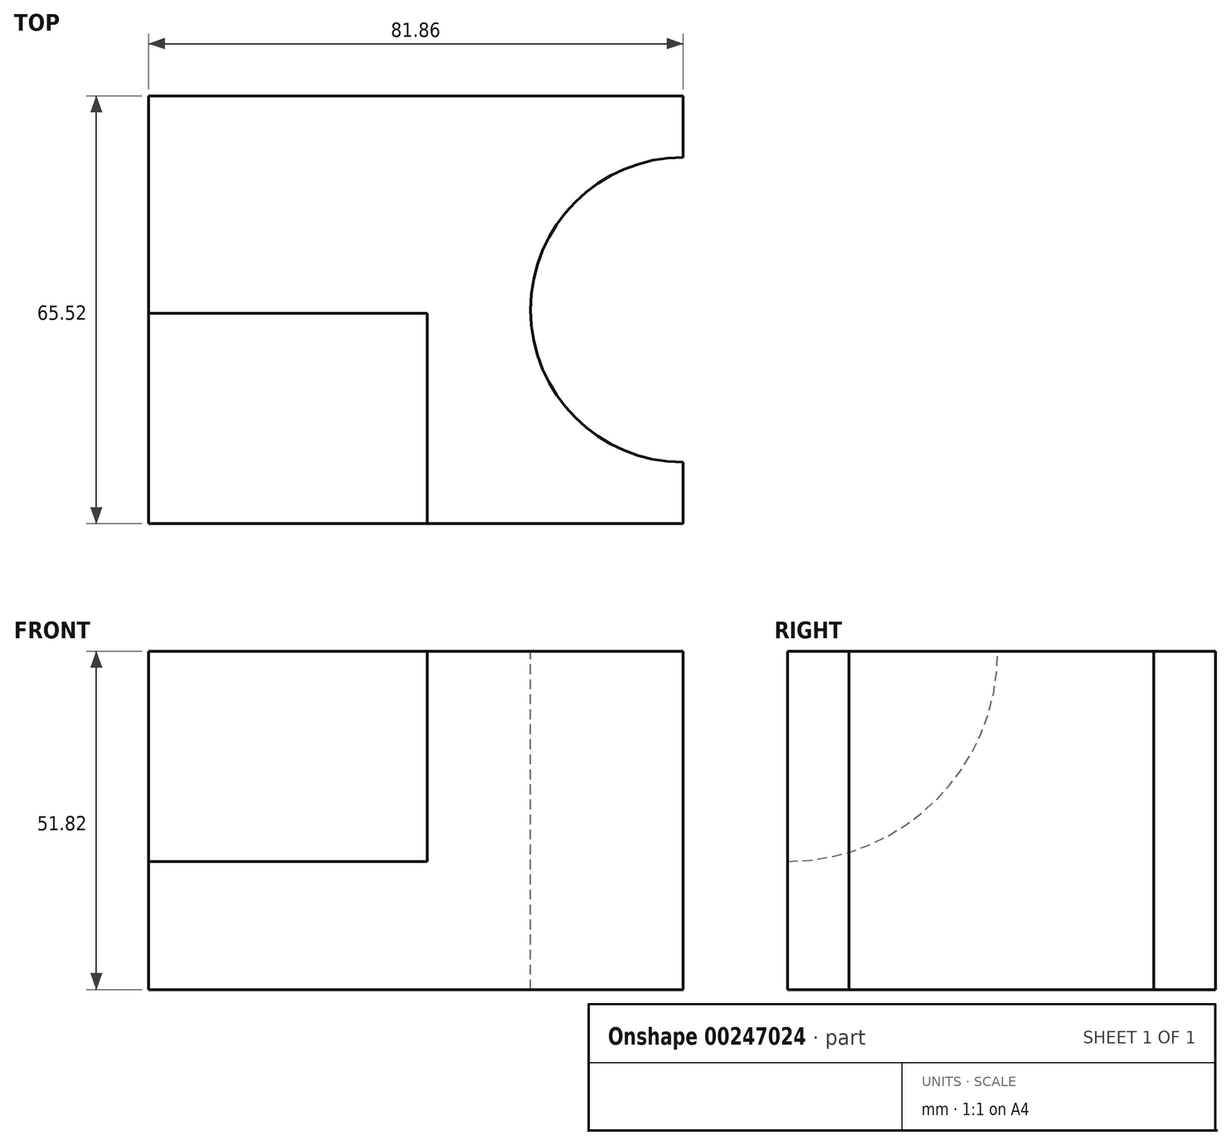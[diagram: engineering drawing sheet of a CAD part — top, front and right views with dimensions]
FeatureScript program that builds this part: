
annotation { "Feature Type Name" : "Feature", "Feature Type Description" : "" }
export const myFeature = defineFeature(function(context is Context, id is Id, definition is map)
    precondition{}
    {
        {
            var Q0;
            Q0=qCreatedBy(makeId("Top.planeOp"),FACE);
            var sketch = newSketch(context, id + "F0", { "sketchPlane" : qUnion([Q0])});
            skLineSegment(sketch, "E0.bottom", {"start": v(-40.93, 32.76) * mm, "end": v(40.93, 32.76) * mm});
            skLineSegment(sketch, "E0.top", {"start": v(-40.93, -32.76) * mm, "end": v(40.93, -32.76) * mm});
            skLineSegment(sketch, "E0.left", {"start": v(-40.93, 32.76) * mm, "end": v(-40.93, -32.76) * mm});
            skLineSegment(sketch, "E0.right", {"start": v(40.93, 32.76) * mm, "end": v(40.93, -32.76) * mm});
            skPoint(sketch, "E0.middle", {"position": v(0, 0) * mm});
            skSolve(sketch);
        }
        {
            var Q0;
            Q0=makeQuery(id+"F0.imprint","IMPRINT",FACE,{"disambiguationData":[TD([[makeQuery(id+"F0.imprint","IMPRINT",EDGE,{"derivedFrom":sQuery(id+"F0.wireOp",EDGE,"E0.bottom")}),-1.0]])]});
            extrude(context, id + "F1", {"entities" : qUnion([Q0]), "depth" : 51.82 * mm});
        }
        {
            var Q0;
            Q0=makeQuery(id+"F1.opExtrude","CAP_FACE",FACE,{"disambiguationData":[OSD([sQuery(id+"F0.wireOp",EDGE,"E0.bottom"),sQuery(id+"F0.wireOp",EDGE,"E0.top"),sQuery(id+"F0.wireOp",EDGE,"E0.left"),sQuery(id+"F0.wireOp",EDGE,"E0.right")])],"isStart":false});
            var sketch = newSketch(context, id + "F2", { "sketchPlane" : qUnion([Q0])});
            skCircle(sketch, "E1", {"center": v(40.93, 0) * mm, "radius": 23.34 * mm});
            skSolve(sketch);
        }
        {
            var Q0;
            {var subQ0=sQuery(id+"F2.wireOp",EDGE,"E1");var subQ1=makeQuery(id+"F1.opExtrude","CAP_EDGE",EDGE,{"disambiguationData":[OSD([sQuery(id+"F0.wireOp",EDGE,"E0.right")])],"isStart":false});var subQ2=makeQuery(id+"F2.imprint","INTERSECT",VERTEX,{"disambiguationData":[OD(0.0)],"derivedFrom":[subQ1,subQ0]});Q0=makeQuery(id+"F2.imprint","IMPRINT",FACE,{"disambiguationData":[TD([[makeQuery(id+"F2.imprint","IMPRINT",EDGE,{"disambiguationData":[TD([[subQ2,-1.0]])],"derivedFrom":subQ0}),1.0]])]});}
            extrude(context, id + "F3", {"entities" : qUnion([Q0]), "operationType" : NewBodyOperationType.REMOVE, "oppositeDirection" : true, "depth" : 79 * mm});
        }
        {
            var Q0;
            Q0=makeQuery(id+"F1.opExtrude","SWEPT_FACE",FACE,{"disambiguationData":[OSD([sQuery(id+"F0.wireOp",EDGE,"E0.left")])]});
            var sketch = newSketch(context, id + "F4", { "sketchPlane" : qUnion([Q0])});
            skCircle(sketch, "E2", {"center": v(32.76, 51.82) * mm, "radius": 32.2 * mm});
            skSolve(sketch);
        }
        {
            var Q0;
            {var subQ0=sQuery(id+"F4.wireOp",EDGE,"E2");var subQ1=sQuery(id+"F0.wireOp",EDGE,"E0.left");var subQ4=makeQuery(id+"F1.opExtrude","CAP_EDGE",EDGE,{"disambiguationData":[OSD([subQ1])],"isStart":false});var subQ5=makeQuery(id+"F4.imprint","INTERSECT",VERTEX,{"derivedFrom":[subQ4,subQ0]});Q0=makeQuery(id+"F4.imprint","IMPRINT",FACE,{"disambiguationData":[TD([[makeQuery(id+"F4.imprint","IMPRINT",EDGE,{"disambiguationData":[TD([[subQ5,1.0]])],"derivedFrom":subQ0}),1.0]])]});}
            var Q1;
            {var subQ0=sQuery(id+"F4.wireOp",EDGE,"E2");var subQ1=sQuery(id+"F0.wireOp",EDGE,"E0.left");var subQ4=makeQuery(id+"F1.opExtrude","CAP_EDGE",EDGE,{"disambiguationData":[OSD([subQ1])],"isStart":false});var subQ5=makeQuery(id+"F4.imprint","INTERSECT",VERTEX,{"derivedFrom":[subQ4,subQ0]});Q1=makeQuery(id+"F4.imprint","IMPRINT",FACE,{"disambiguationData":[TD([[makeQuery(id+"F4.imprint","IMPRINT",EDGE,{"disambiguationData":[TD([[subQ5,-1.0]])],"derivedFrom":subQ0}),1.0]])]});}
            extrude(context, id + "F5", {"entities" : qUnion([Q0, Q1]), "operationType" : NewBodyOperationType.REMOVE, "oppositeDirection" : true, "depth" : 42.67 * mm});
        }
    });
